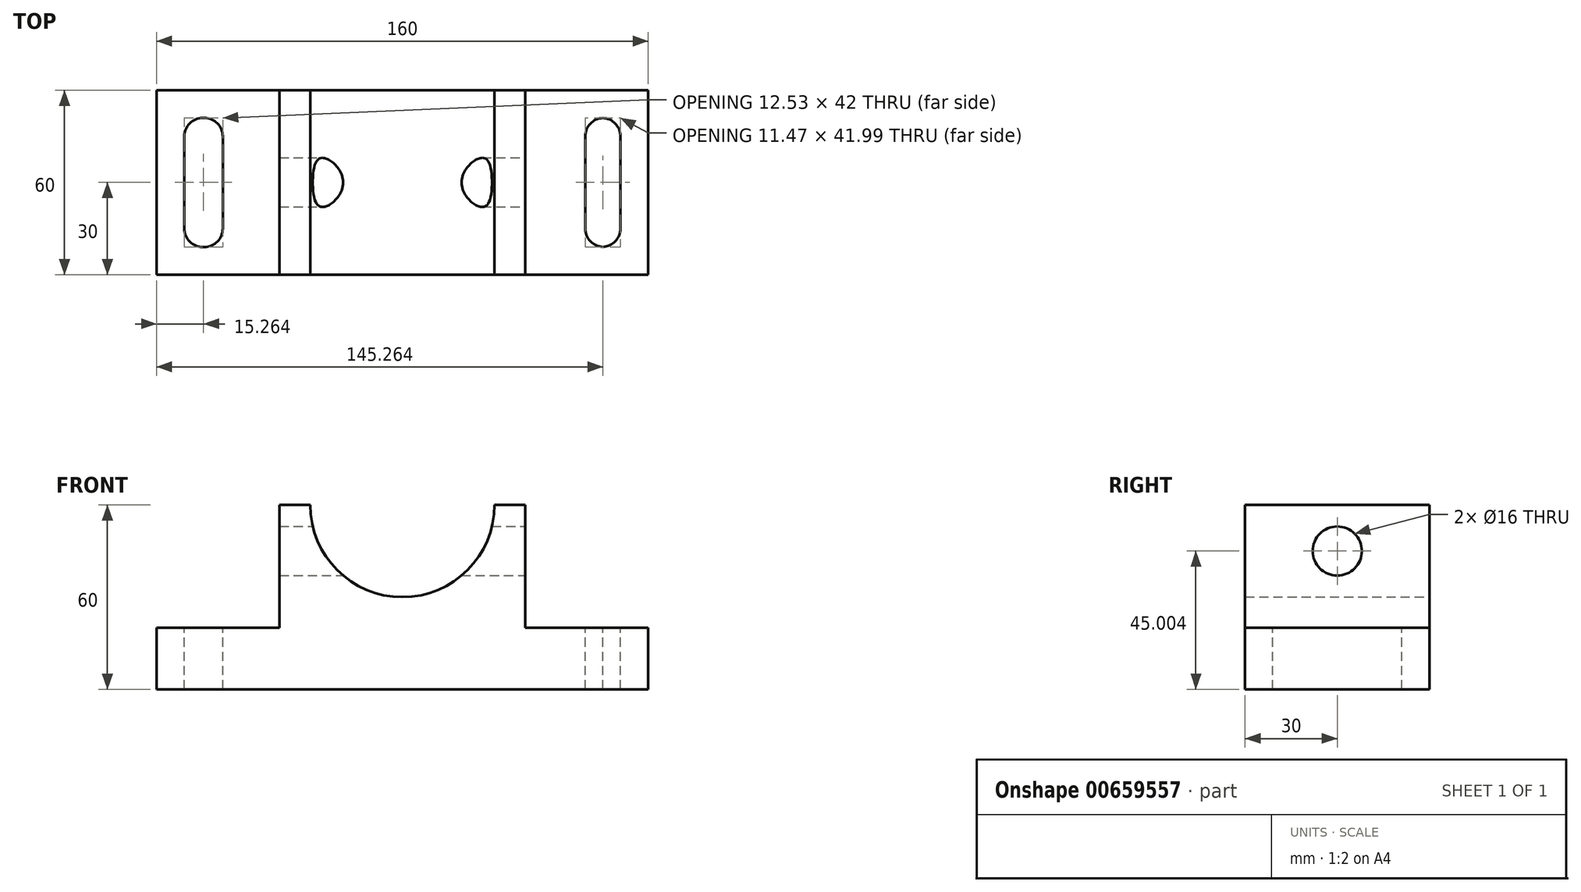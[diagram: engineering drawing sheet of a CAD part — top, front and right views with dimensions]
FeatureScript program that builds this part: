
annotation { "Feature Type Name" : "Feature", "Feature Type Description" : "" }
export const myFeature = defineFeature(function(context is Context, id is Id, definition is map)
    precondition{}
    {
        {
            var Q0;
            Q0=qCreatedBy(makeId("Front.planeOp"),FACE);
            var sketch = newSketch(context, id + "F0", { "sketchPlane" : qUnion([Q0])});
            skLineSegment(sketch, "E0.top", {"start": v(80, -39.27) * mm, "end": v(-80, -39.27) * mm});
            skLineSegment(sketch, "E0.left", {"start": v(80, -19.27) * mm, "end": v(80, -39.27) * mm});
            skLineSegment(sketch, "E0.right", {"start": v(-80, -19.27) * mm, "end": v(-80, -39.27) * mm});
            skPoint(sketch, "E0.middle", {"position": v(0, -2.2) * mm});
            skLineSegment(sketch, "E1", {"start": v(-80, -39.27) * mm, "end": v(-80, -19.27) * mm});
            skLineSegment(sketch, "E2", {"start": v(-80, -19.27) * mm, "end": v(-40, -19.27) * mm});
            skLineSegment(sketch, "E3", {"start": v(-40, -19.27) * mm, "end": v(-40, 20.73) * mm});
            skLineSegment(sketch, "E4", {"start": v(-40, 20.73) * mm, "end": v(-30, 20.73) * mm});
            skLineSegment(sketch, "E5", {"start": v(40, 20.73) * mm, "end": v(40, -19.27) * mm});
            skLineSegment(sketch, "E6", {"start": v(40, -19.27) * mm, "end": v(80, -19.27) * mm});
            skArc(sketch, "E7", {"start": v(-30, 20.73) * mm, "mid": v(0, -9.27) * mm, "end": v(30, 20.73) * mm});
            skLineSegment(sketch, "E8.trimOffspring", {"start": v(30, 20.73) * mm, "end": v(40, 20.73) * mm});
            skSolve(sketch);
        }
        {
            var Q0;
            Q0=makeQuery(id+"F0.imprint","IMPRINT",FACE,{"disambiguationData":[TD([[makeQuery(id+"F0.imprint","IMPRINT",EDGE,{"derivedFrom":sQuery(id+"F0.wireOp",EDGE,"E0.top")}),-1.0]])]});
            extrude(context, id + "F1", {"entities" : qUnion([Q0]), "endBound" : BoundingType.SYMMETRIC, "depth" : 60 * mm, "offsetDistance" : 25 * mm});
        }
        {
            var Q0;
            Q0=makeQuery(id+"F1.opExtrude","SWEPT_FACE",FACE,{"disambiguationData":[OSD([sQuery(id+"F0.wireOp",EDGE,"E5")])]});
            var sketch = newSketch(context, id + "F2", { "sketchPlane" : qUnion([Q0])});
            skCircle(sketch, "E9", {"center": v(0, 5.73) * mm, "radius": 8 * mm});
            skSolve(sketch);
        }
        {
            var Q0;
            Q0=makeQuery(id+"F2.imprint","IMPRINT",FACE,{"disambiguationData":[TD([[makeQuery(id+"F2.imprint","IMPRINT",EDGE,{"derivedFrom":sQuery(id+"F2.wireOp",EDGE,"E9")}),1.0]])]});
            extrude(context, id + "F3", {"entities" : qUnion([Q0]), "operationType" : NewBodyOperationType.REMOVE, "endBound" : BoundingType.THROUGH_ALL, "oppositeDirection" : true, "depth" : 25 * mm, "offsetDistance" : 25 * mm});
        }
        {
            var Q0;
            Q0=makeQuery(id+"F1.opExtrude","SWEPT_FACE",FACE,{"disambiguationData":[OSD([sQuery(id+"F0.wireOp",EDGE,"E2")])]});
            var sketch = newSketch(context, id + "F4", { "sketchPlane" : qUnion([Q0])});
            skLineSegment(sketch, "E10.bottom", {"start": v(-64.47, 21) * mm, "end": v(-65, 21) * mm});
            skLineSegment(sketch, "E10.top", {"start": v(-64.47, -21) * mm, "end": v(-65, -21) * mm});
            skLineSegment(sketch, "E10.left", {"start": v(-58.47, 15) * mm, "end": v(-58.47, -15) * mm});
            skLineSegment(sketch, "E10.right", {"start": v(-71, 15) * mm, "end": v(-71, -15) * mm});
            skPoint(sketch, "E11.visualSharp", {"position": v(-71, 21) * mm});
            skArc(sketch, "E11.filletArc", {"start": v(-65, 21) * mm, "mid": v(-69.24, 19.24) * mm, "end": v(-71, 15) * mm});
            skPoint(sketch, "E12.visualSharp", {"position": v(-58.47, 21) * mm});
            skArc(sketch, "E12.filletArc", {"start": v(-58.47, 15) * mm, "mid": v(-60.23, 19.24) * mm, "end": v(-64.47, 21) * mm});
            skPoint(sketch, "E13.visualSharp", {"position": v(-58.47, -21) * mm});
            skArc(sketch, "E13.filletArc", {"start": v(-64.47, -21) * mm, "mid": v(-60.23, -19.24) * mm, "end": v(-58.47, -15) * mm});
            skPoint(sketch, "E14.visualSharp", {"position": v(-71, -21) * mm});
            skArc(sketch, "E14.filletArc", {"start": v(-71, -15) * mm, "mid": v(-69.24, -19.24) * mm, "end": v(-65, -21) * mm});
            skLineSegment(sketch, "E15", {"start": v(-80, 30) * mm, "end": v(-80, -30) * mm});
            skLineSegment(sketch, "E16", {"start": v(-80, -30) * mm, "end": v(-40, -30) * mm});
            skSolve(sketch);
        }
        {
            var Q0;
            Q0=makeQuery(id+"F4.imprint","IMPRINT",FACE,{"disambiguationData":[TD([[makeQuery(id+"F4.imprint","IMPRINT",EDGE,{"derivedFrom":sQuery(id+"F4.wireOp",EDGE,"E10.bottom")}),1.0]])]});
            extrude(context, id + "F5", {"entities" : qUnion([Q0]), "operationType" : NewBodyOperationType.REMOVE, "endBound" : BoundingType.THROUGH_ALL, "oppositeDirection" : true, "depth" : 25 * mm, "offsetDistance" : 25 * mm});
        }
        {
            var Q0;
            Q0=makeQuery(id+"F1.opExtrude","SWEPT_FACE",FACE,{"disambiguationData":[OSD([sQuery(id+"F0.wireOp",EDGE,"E6")])]});
            var sketch = newSketch(context, id + "F6", { "sketchPlane" : qUnion([Q0])});
            skLineSegment(sketch, "E17.bottom", {"start": v(65.53, 21) * mm, "end": v(65, 21) * mm});
            skLineSegment(sketch, "E17.top", {"start": v(65.53, -21) * mm, "end": v(65, -21) * mm});
            skLineSegment(sketch, "E17.left", {"start": v(71, 15) * mm, "end": v(71, -15) * mm});
            skLineSegment(sketch, "E17.right", {"start": v(59.53, 15) * mm, "end": v(59.53, -15) * mm});
            skPoint(sketch, "E18.visualSharp", {"position": v(59.53, 21) * mm});
            skArc(sketch, "E18.filletArc", {"start": v(65.53, 21) * mm, "mid": v(61.29, 19.24) * mm, "end": v(59.53, 15) * mm});
            skPoint(sketch, "E19.visualSharp", {"position": v(71, 21) * mm});
            skArc(sketch, "E19.filletArc", {"start": v(71, 15) * mm, "mid": v(69.24, 19.24) * mm, "end": v(65, 21) * mm});
            skPoint(sketch, "E20.visualSharp", {"position": v(71, -21) * mm});
            skArc(sketch, "E20.filletArc", {"start": v(65, -21) * mm, "mid": v(69.24, -19.24) * mm, "end": v(71, -15) * mm});
            skPoint(sketch, "E21.visualSharp", {"position": v(59.53, -21) * mm});
            skArc(sketch, "E21.filletArc", {"start": v(59.53, -15) * mm, "mid": v(61.29, -19.24) * mm, "end": v(65.53, -21) * mm});
            skLineSegment(sketch, "E22", {"start": v(-80, -30) * mm, "end": v(80, -30) * mm});
            skSolve(sketch);
        }
        {
            var Q0;
            {var subQ1=sQuery(id+"F6.wireOp",EDGE,"E17.left");Q0=makeQuery(id+"F6.imprint","IMPRINT",FACE,{"disambiguationData":[TD([[makeQuery(id+"F6.imprint","IMPRINT",EDGE,{"derivedFrom":subQ1}),-1.0]])]});}
            extrude(context, id + "F7", {"entities" : qUnion([Q0]), "operationType" : NewBodyOperationType.REMOVE, "endBound" : BoundingType.THROUGH_ALL, "oppositeDirection" : true, "depth" : 25 * mm, "offsetDistance" : 25 * mm});
        }
    });
